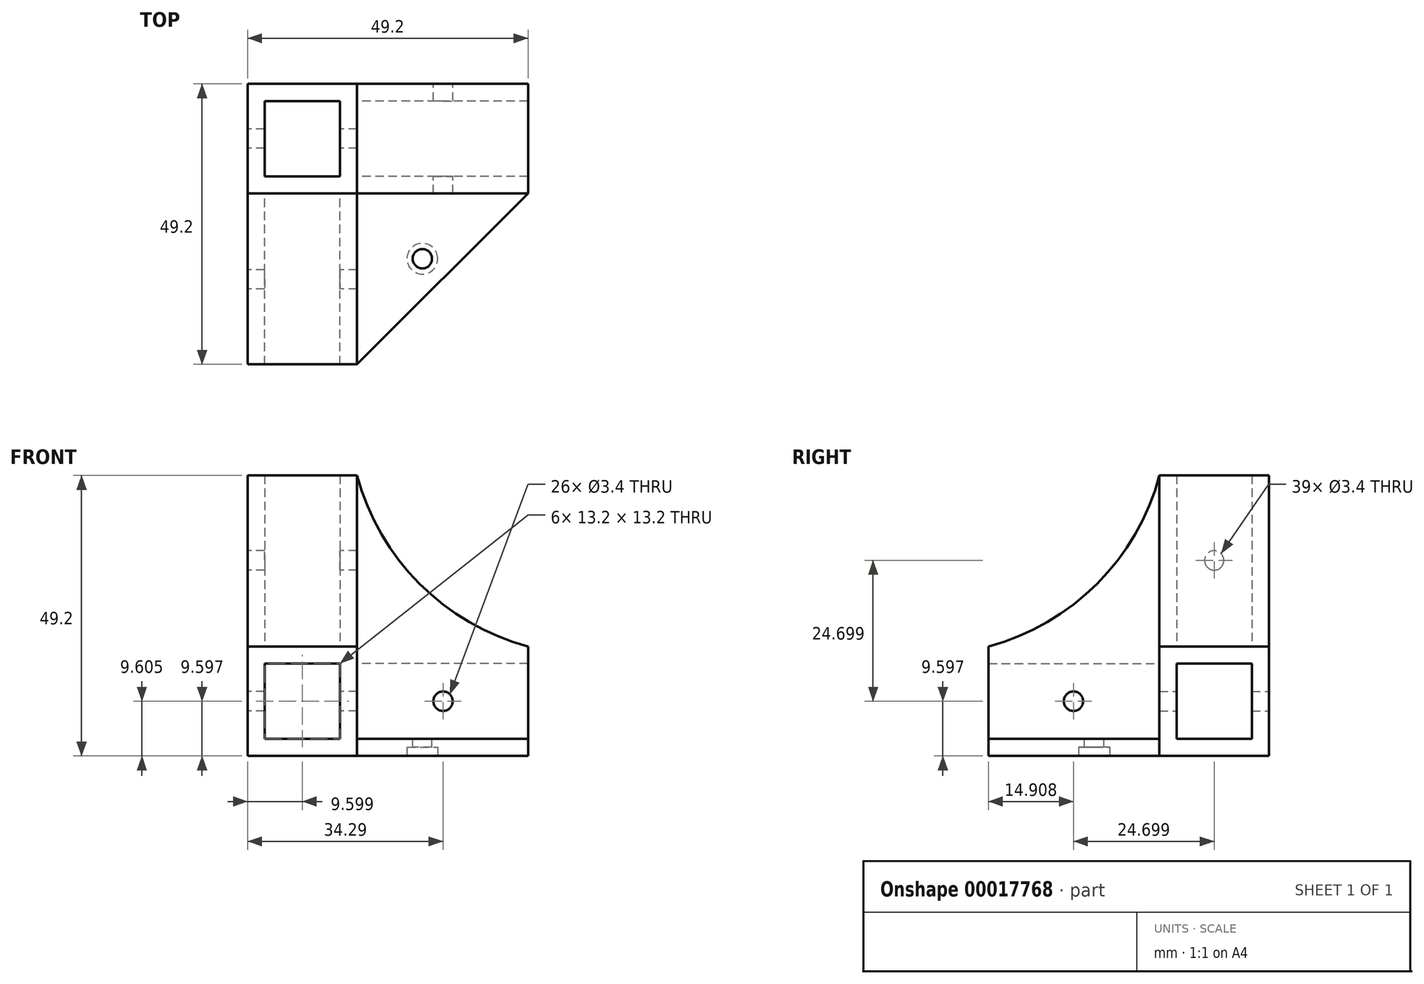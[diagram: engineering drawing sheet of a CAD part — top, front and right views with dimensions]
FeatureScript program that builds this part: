
annotation { "Feature Type Name" : "Feature", "Feature Type Description" : "" }
export const myFeature = defineFeature(function(context is Context, id is Id, definition is map)
    precondition{}
    {
        {
            var Q0;
            Q0=qCreatedBy(makeId("Front.planeOp"),FACE);
            var sketch = newSketch(context, id + "F0", { "sketchPlane" : qUnion([Q0])});
            skLineSegment(sketch, "E0.bottom", {"start": v(-58, 0.4) * mm, "end": v(-44.8, 0.4) * mm});
            skLineSegment(sketch, "E0.top", {"start": v(-58, -12.8) * mm, "end": v(-44.8, -12.8) * mm});
            skLineSegment(sketch, "E0.left", {"start": v(-58, 0.4) * mm, "end": v(-58, -12.8) * mm});
            skLineSegment(sketch, "E0.right", {"start": v(-44.8, 0.4) * mm, "end": v(-44.8, -12.8) * mm});
            skLineSegment(sketch, "E1.0", {"start": v(-61, 3.4) * mm, "end": v(-41.8, 3.4) * mm});
            skLineSegment(sketch, "E1.1", {"start": v(-61, 3.4) * mm, "end": v(-61, -15.8) * mm});
            skLineSegment(sketch, "E1.2", {"start": v(-61, -15.8) * mm, "end": v(-41.8, -15.8) * mm});
            skLineSegment(sketch, "E1.3", {"start": v(-41.8, 3.4) * mm, "end": v(-41.8, -15.8) * mm});
            skSolve(sketch);
        }
        {
            var Q0;
            Q0=makeQuery(id+"F0.imprint","IMPRINT",FACE,{"disambiguationData":[TD([[makeQuery(id+"F0.imprint","IMPRINT",EDGE,{"derivedFrom":sQuery(id+"F0.wireOp",EDGE,"E0.bottom")}),1.0]])]});
            extrude(context, id + "F1", {"entities" : qUnion([Q0]), "depth" : 30 * mm});
        }
        {
            var Q0;
            Q0=makeQuery(id+"F1.opExtrude","SWEPT_FACE",FACE,{"disambiguationData":[OSD([sQuery(id+"F0.wireOp",EDGE,"E1.1")])]});
            var sketch = newSketch(context, id + "F2", { "sketchPlane" : qUnion([Q0])});
            skCircle(sketch, "E2", {"center": v(15.1, -6.2) * mm, "radius": 1.7 * mm});
            skSolve(sketch);
        }
        {
            var Q0;
            Q0=makeQuery(id+"F2.imprint","IMPRINT",FACE,{"disambiguationData":[TD([[makeQuery(id+"F2.imprint","IMPRINT",EDGE,{"derivedFrom":sQuery(id+"F2.wireOp",EDGE,"E2")}),1.0]])]});
            extrude(context, id + "F3", {"entities" : qUnion([Q0]), "operationType" : NewBodyOperationType.REMOVE, "oppositeDirection" : true, "depth" : 25 * mm});
        }
        {
            var Q0;
            Q0=makeQuery(id+"F1.opExtrude","SWEPT_BODY",BODY,{"disambiguationData":[OSD([sQuery(id+"F0.wireOp",EDGE,"E0.bottom"),sQuery(id+"F0.wireOp",EDGE,"E0.top"),sQuery(id+"F0.wireOp",EDGE,"E0.left"),sQuery(id+"F0.wireOp",EDGE,"E0.right"),sQuery(id+"F0.wireOp",EDGE,"E1.0"),sQuery(id+"F0.wireOp",EDGE,"E1.1"),sQuery(id+"F0.wireOp",EDGE,"E1.2"),sQuery(id+"F0.wireOp",EDGE,"E1.3")])]});
            var Q1;
            Q1=makeQuery(id+"F1.opExtrude","CAP_EDGE",EDGE,{"disambiguationData":[OSD([sQuery(id+"F0.wireOp",EDGE,"E1.3")])],"isStart":true});
            transform(context, id + "F4", {"entities" : qUnion([Q0]), "transformType" : TransformType.ROTATION, "transformAxis" : qUnion([Q1]), "angle" : 90 * degree, "oppositeDirection" : true, "makeCopy" : true});
        }
        {
            var Q0;
            Q0=makeQuery(id+"F1.opExtrude","SWEPT_BODY",BODY,{"disambiguationData":[OSD([sQuery(id+"F0.wireOp",EDGE,"E0.bottom"),sQuery(id+"F0.wireOp",EDGE,"E0.top"),sQuery(id+"F0.wireOp",EDGE,"E0.left"),sQuery(id+"F0.wireOp",EDGE,"E0.right"),sQuery(id+"F0.wireOp",EDGE,"E1.0"),sQuery(id+"F0.wireOp",EDGE,"E1.1"),sQuery(id+"F0.wireOp",EDGE,"E1.2"),sQuery(id+"F0.wireOp",EDGE,"E1.3")])]});
            var Q1;
            Q1=makeQuery(id+"F1.opExtrude","CAP_EDGE",EDGE,{"disambiguationData":[OSD([sQuery(id+"F0.wireOp",EDGE,"E1.0")])],"isStart":true});
            transform(context, id + "F5", {"entities" : qUnion([Q0]), "transformType" : TransformType.ROTATION, "transformAxis" : qUnion([Q1]), "angle" : 90 * degree, "oppositeDirection" : true, "makeCopy" : true});
        }
        {
            var Q0;
            Q0=makeQuery(id+"F4.opPattern","COPY",BODY,{"derivedFrom":makeQuery(id+"F1.opExtrude","SWEPT_BODY",BODY,{"disambiguationData":[OSD([sQuery(id+"F0.wireOp",EDGE,"E0.bottom"),sQuery(id+"F0.wireOp",EDGE,"E0.top"),sQuery(id+"F0.wireOp",EDGE,"E0.left"),sQuery(id+"F0.wireOp",EDGE,"E0.right"),sQuery(id+"F0.wireOp",EDGE,"E1.0"),sQuery(id+"F0.wireOp",EDGE,"E1.1"),sQuery(id+"F0.wireOp",EDGE,"E1.2"),sQuery(id+"F0.wireOp",EDGE,"E1.3")])]}),"instanceName":"1"});
            var Q1;
            Q1=makeQuery(id+"F4.opPattern","COPY",FACE,{"derivedFrom":makeQuery(id+"F1.opExtrude","SWEPT_FACE",FACE,{"disambiguationData":[OSD([sQuery(id+"F0.wireOp",EDGE,"E1.3")])]}),"instanceName":"1"});
            mirror(context, id + "F6", {"entities" : qUnion([Q0]), "mirrorPlane" : qUnion([Q1])});
        }
        {
            var Q0;
            Q0=makeQuery(id+"F4.opPattern","COPY",BODY,{"derivedFrom":makeQuery(id+"F1.opExtrude","SWEPT_BODY",BODY,{"disambiguationData":[OSD([sQuery(id+"F0.wireOp",EDGE,"E0.bottom"),sQuery(id+"F0.wireOp",EDGE,"E0.top"),sQuery(id+"F0.wireOp",EDGE,"E0.left"),sQuery(id+"F0.wireOp",EDGE,"E0.right"),sQuery(id+"F0.wireOp",EDGE,"E1.0"),sQuery(id+"F0.wireOp",EDGE,"E1.1"),sQuery(id+"F0.wireOp",EDGE,"E1.2"),sQuery(id+"F0.wireOp",EDGE,"E1.3")])]}),"instanceName":"1"});
            deleteBodies(context, id + "F7", {"entities" : qUnion([Q0])});
        }
        {
            var Q0;
            Q0=makeQuery(id+"F5.opPattern","COPY",BODY,{"derivedFrom":makeQuery(id+"F1.opExtrude","SWEPT_BODY",BODY,{"disambiguationData":[OSD([sQuery(id+"F0.wireOp",EDGE,"E0.bottom"),sQuery(id+"F0.wireOp",EDGE,"E0.top"),sQuery(id+"F0.wireOp",EDGE,"E0.left"),sQuery(id+"F0.wireOp",EDGE,"E0.right"),sQuery(id+"F0.wireOp",EDGE,"E1.0"),sQuery(id+"F0.wireOp",EDGE,"E1.1"),sQuery(id+"F0.wireOp",EDGE,"E1.2"),sQuery(id+"F0.wireOp",EDGE,"E1.3")])]}),"instanceName":"1"});
            var Q1;
            Q1=qCreatedBy(makeId("Front.planeOp"),FACE);
            mirror(context, id + "F8", {"entities" : qUnion([Q0]), "mirrorPlane" : qUnion([Q1])});
        }
        {
            var Q0;
            Q0=makeQuery(id+"F5.opPattern","COPY",BODY,{"derivedFrom":makeQuery(id+"F1.opExtrude","SWEPT_BODY",BODY,{"disambiguationData":[OSD([sQuery(id+"F0.wireOp",EDGE,"E0.bottom"),sQuery(id+"F0.wireOp",EDGE,"E0.top"),sQuery(id+"F0.wireOp",EDGE,"E0.left"),sQuery(id+"F0.wireOp",EDGE,"E0.right"),sQuery(id+"F0.wireOp",EDGE,"E1.0"),sQuery(id+"F0.wireOp",EDGE,"E1.1"),sQuery(id+"F0.wireOp",EDGE,"E1.2"),sQuery(id+"F0.wireOp",EDGE,"E1.3")])]}),"instanceName":"1"});
            deleteBodies(context, id + "F9", {"entities" : qUnion([Q0])});
        }
        {
            var Q0;
            Q0=makeQuery(id+"F0.imprint","IMPRINT",FACE,{"disambiguationData":[TD([[makeQuery(id+"F0.imprint","IMPRINT",EDGE,{"derivedFrom":sQuery(id+"F0.wireOp",EDGE,"E0.bottom")}),1.0]])]});
            var Q1;
            Q1=sQuery(id+"F0.wireOp",EDGE,"E1.1");
            var Q2;
            Q2=sQuery(id+"F0.wireOp",EDGE,"E1.0");
            var Q3;
            Q3=sQuery(id+"F0.wireOp",EDGE,"E1.3");
            var Q4;
            Q4=sQuery(id+"F0.wireOp",EDGE,"E1.2");
            var Q5;
            Q5=makeQuery(id+"F8.opPattern","COPY",FACE,{"derivedFrom":makeQuery(id+"F5.opPattern","COPY",FACE,{"derivedFrom":makeQuery(id+"F1.opExtrude","SWEPT_FACE",FACE,{"disambiguationData":[OSD([sQuery(id+"F0.wireOp",EDGE,"E1.2")])]}),"instanceName":"1"}),"instanceName":"1"});
            extrude(context, id + "F10", {"entities" : qUnion([Q0]), "surfaceEntities" : qUnion([Q1, Q2, Q3, Q4]), "endBound" : BoundingType.UP_TO_SURFACE, "oppositeDirection" : true, "endBoundEntityFace" : qUnion([Q5]), "depth" : 21.53 * mm});
        }
        {
            var Q0;
            Q0=makeQuery(id+"F0.imprint","IMPRINT",FACE,{"disambiguationData":[TD([[makeQuery(id+"F0.imprint","IMPRINT",EDGE,{"derivedFrom":sQuery(id+"F0.wireOp",EDGE,"E0.bottom")}),-1.0]])]});
            var Q1;
            Q1=makeQuery(id+"F10.opExtrude","CAP_FACE",FACE,{"disambiguationData":[OSD([sQuery(id+"F0.wireOp",EDGE,"E0.bottom"),sQuery(id+"F0.wireOp",EDGE,"E0.top"),sQuery(id+"F0.wireOp",EDGE,"E0.left"),sQuery(id+"F0.wireOp",EDGE,"E0.right"),sQuery(id+"F0.wireOp",EDGE,"E1.0"),sQuery(id+"F0.wireOp",EDGE,"E1.1"),sQuery(id+"F0.wireOp",EDGE,"E1.2"),sQuery(id+"F0.wireOp",EDGE,"E1.3")])],"isStart":false});
            extrude(context, id + "F11", {"entities" : qUnion([Q0]), "endBound" : BoundingType.UP_TO_SURFACE, "oppositeDirection" : true, "endBoundEntityFace" : qUnion([Q1]), "depth" : 25 * mm});
        }
        {
            var Q0;
            Q0=makeQuery(id+"F10.opExtrude","SWEPT_FACE",FACE,{"disambiguationData":[OSD([sQuery(id+"F0.wireOp",EDGE,"E1.1")])]});
            var sketch = newSketch(context, id + "F12", { "sketchPlane" : qUnion([Q0])});
            skArc(sketch, "E3", {"start": v(0, 33.4) * mm, "mid": v(10.97, 14.38) * mm, "end": v(30, 3.4) * mm});
            skLineSegment(sketch, "E4", {"start": v(0, 33.4) * mm, "end": v(0, 3.4) * mm});
            skLineSegment(sketch, "E5", {"start": v(0, 3.4) * mm, "end": v(30, 3.4) * mm});
            skSolve(sketch);
        }
        {
            var Q0;
            Q0=makeQuery(id+"F12.imprint","IMPRINT",FACE,{"disambiguationData":[TD([[makeQuery(id+"F12.imprint","IMPRINT",EDGE,{"derivedFrom":sQuery(id+"F12.wireOp",EDGE,"E3")}),-1.0]])]});
            var Q1;
            Q1=makeQuery(id+"F8.opPattern","COPY",FACE,{"derivedFrom":makeQuery(id+"F5.opPattern","COPY",FACE,{"derivedFrom":makeQuery(id+"F1.opExtrude","SWEPT_FACE",FACE,{"disambiguationData":[OSD([sQuery(id+"F0.wireOp",EDGE,"E1.3")])]}),"instanceName":"1"}),"instanceName":"1"});
            extrude(context, id + "F13", {"entities" : qUnion([Q0]), "endBound" : BoundingType.UP_TO_SURFACE, "oppositeDirection" : true, "endBoundEntityFace" : qUnion([Q1]), "depth" : 25 * mm});
        }
        {
            var Q0;
            Q0=makeQuery(id+"F13.opExtrude","SWEPT_BODY",BODY,{"disambiguationData":[OSD([sQuery(id+"F12.wireOp",EDGE,"E3"),sQuery(id+"F12.wireOp",EDGE,"E4"),sQuery(id+"F12.wireOp",EDGE,"E5")])]});
            var Q1;
            Q1=makeQuery(id+"F8.opPattern","COPY",EDGE,{"derivedFrom":makeQuery(id+"F5.opPattern","COPY",EDGE,{"derivedFrom":makeQuery(id+"F1.opExtrude","SWEPT_EDGE",EDGE,{"disambiguationData":[OSD([sQuery(id+"F0.wireOp",EDGE,"E1.0"),sQuery(id+"F0.wireOp",EDGE,"E1.3")])]}),"instanceName":"1"}),"instanceName":"1"});
            transform(context, id + "F14", {"entities" : qUnion([Q0]), "transformType" : TransformType.ROTATION, "transformAxis" : qUnion([Q1]), "angle" : 90 * degree, "oppositeDirection" : true, "makeCopy" : true});
        }
        {
            var Q0;
            Q0=makeQuery(id+"F14.opPattern","COPY",FACE,{"derivedFrom":makeQuery(id+"F13.opExtrude","CAP_FACE",FACE,{"disambiguationData":[OSD([sQuery(id+"F12.wireOp",EDGE,"E3"),sQuery(id+"F12.wireOp",EDGE,"E4"),sQuery(id+"F12.wireOp",EDGE,"E5")])],"isStart":false}),"instanceName":"1"});
            var Q1;
            Q1=makeQuery(id+"F8.opPattern","COPY",FACE,{"derivedFrom":makeQuery(id+"F5.opPattern","COPY",FACE,{"derivedFrom":makeQuery(id+"F1.opExtrude","SWEPT_FACE",FACE,{"disambiguationData":[OSD([sQuery(id+"F0.wireOp",EDGE,"E1.2")])]}),"instanceName":"1"}),"instanceName":"1"});
            var Q2;
            Q2=makeQuery(id+"F6.opPattern","COPY",BODY,{"derivedFrom":makeQuery(id+"F4.opPattern","COPY",BODY,{"derivedFrom":makeQuery(id+"F1.opExtrude","SWEPT_BODY",BODY,{"disambiguationData":[OSD([sQuery(id+"F0.wireOp",EDGE,"E0.bottom"),sQuery(id+"F0.wireOp",EDGE,"E0.top"),sQuery(id+"F0.wireOp",EDGE,"E0.left"),sQuery(id+"F0.wireOp",EDGE,"E0.right"),sQuery(id+"F0.wireOp",EDGE,"E1.0"),sQuery(id+"F0.wireOp",EDGE,"E1.1"),sQuery(id+"F0.wireOp",EDGE,"E1.2"),sQuery(id+"F0.wireOp",EDGE,"E1.3")])]}),"instanceName":"1"}),"instanceName":"1"});
            extrude(context, id + "F15", {"entities" : qUnion([Q0]), "endBound" : BoundingType.UP_TO_SURFACE, "endBoundEntityFace" : qUnion([Q1]), "endBoundEntityBody" : qUnion([Q2]), "depth" : 30 * mm});
        }
        {
            var Q0;
            Q0=makeQuery(id+"F14.opPattern","COPY",BODY,{"derivedFrom":makeQuery(id+"F13.opExtrude","SWEPT_BODY",BODY,{"disambiguationData":[OSD([sQuery(id+"F12.wireOp",EDGE,"E3"),sQuery(id+"F12.wireOp",EDGE,"E4"),sQuery(id+"F12.wireOp",EDGE,"E5")])]}),"instanceName":"1"});
            deleteBodies(context, id + "F16", {"entities" : qUnion([Q0])});
        }
        {
            var Q0;
            Q0=makeQuery(id+"F1.opExtrude","SWEPT_FACE",FACE,{"disambiguationData":[OSD([sQuery(id+"F0.wireOp",EDGE,"E1.2")])]});
            var sketch = newSketch(context, id + "F17", { "sketchPlane" : qUnion([Q0])});
            skLineSegment(sketch, "E6", {"start": v(-41.8, 30) * mm, "end": v(-11.8, 0) * mm});
            skLineSegment(sketch, "E7", {"start": v(-11.8, 0) * mm, "end": v(-41.8, 0) * mm});
            skLineSegment(sketch, "E8", {"start": v(-41.8, 0) * mm, "end": v(-41.8, 30) * mm});
            skSolve(sketch);
        }
        {
            var Q0;
            Q0=makeQuery(id+"F17.imprint","IMPRINT",FACE,{"disambiguationData":[TD([[makeQuery(id+"F17.imprint","IMPRINT",EDGE,{"derivedFrom":sQuery(id+"F17.wireOp",EDGE,"E6")}),-1.0]])]});
            extrude(context, id + "F18", {"entities" : qUnion([Q0]), "oppositeDirection" : true, "depth" : 3 * mm});
        }
        {
            var Q0;
            Q0=makeQuery(id+"F8.opPattern","COPY",BODY,{"derivedFrom":makeQuery(id+"F5.opPattern","COPY",BODY,{"derivedFrom":makeQuery(id+"F1.opExtrude","SWEPT_BODY",BODY,{"disambiguationData":[OSD([sQuery(id+"F0.wireOp",EDGE,"E0.bottom"),sQuery(id+"F0.wireOp",EDGE,"E0.top"),sQuery(id+"F0.wireOp",EDGE,"E0.left"),sQuery(id+"F0.wireOp",EDGE,"E0.right"),sQuery(id+"F0.wireOp",EDGE,"E1.0"),sQuery(id+"F0.wireOp",EDGE,"E1.1"),sQuery(id+"F0.wireOp",EDGE,"E1.2"),sQuery(id+"F0.wireOp",EDGE,"E1.3")])]}),"instanceName":"1"}),"instanceName":"1"});
            var Q1;
            Q1=makeQuery(id+"F13.opExtrude","SWEPT_BODY",BODY,{"disambiguationData":[OSD([sQuery(id+"F12.wireOp",EDGE,"E3"),sQuery(id+"F12.wireOp",EDGE,"E4"),sQuery(id+"F12.wireOp",EDGE,"E5")])]});
            var Q2;
            Q2=makeQuery(id+"F15.opExtrude","SWEPT_BODY",BODY,{"disambiguationData":[OSD([sQuery(id+"F12.wireOp",EDGE,"E3"),sQuery(id+"F12.wireOp",EDGE,"E4"),sQuery(id+"F12.wireOp",EDGE,"E5")])]});
            var Q3;
            Q3=makeQuery(id+"F6.opPattern","COPY",BODY,{"derivedFrom":makeQuery(id+"F4.opPattern","COPY",BODY,{"derivedFrom":makeQuery(id+"F1.opExtrude","SWEPT_BODY",BODY,{"disambiguationData":[OSD([sQuery(id+"F0.wireOp",EDGE,"E0.bottom"),sQuery(id+"F0.wireOp",EDGE,"E0.top"),sQuery(id+"F0.wireOp",EDGE,"E0.left"),sQuery(id+"F0.wireOp",EDGE,"E0.right"),sQuery(id+"F0.wireOp",EDGE,"E1.0"),sQuery(id+"F0.wireOp",EDGE,"E1.1"),sQuery(id+"F0.wireOp",EDGE,"E1.2"),sQuery(id+"F0.wireOp",EDGE,"E1.3")])]}),"instanceName":"1"}),"instanceName":"1"});
            var Q4;
            Q4=makeQuery(id+"F1.opExtrude","SWEPT_BODY",BODY,{"disambiguationData":[OSD([sQuery(id+"F0.wireOp",EDGE,"E0.bottom"),sQuery(id+"F0.wireOp",EDGE,"E0.top"),sQuery(id+"F0.wireOp",EDGE,"E0.left"),sQuery(id+"F0.wireOp",EDGE,"E0.right"),sQuery(id+"F0.wireOp",EDGE,"E1.0"),sQuery(id+"F0.wireOp",EDGE,"E1.1"),sQuery(id+"F0.wireOp",EDGE,"E1.2"),sQuery(id+"F0.wireOp",EDGE,"E1.3")])]});
            var Q5;
            Q5=makeQuery(id+"F18.opExtrude","SWEPT_BODY",BODY,{"disambiguationData":[OSD([sQuery(id+"F17.wireOp",EDGE,"E6"),sQuery(id+"F17.wireOp",EDGE,"E7"),sQuery(id+"F17.wireOp",EDGE,"E8")])]});
            var Q6;
            Q6=makeQuery(id+"F10.opExtrude","SWEPT_BODY",BODY,{"disambiguationData":[OSD([sQuery(id+"F0.wireOp",EDGE,"E0.bottom"),sQuery(id+"F0.wireOp",EDGE,"E0.top"),sQuery(id+"F0.wireOp",EDGE,"E0.left"),sQuery(id+"F0.wireOp",EDGE,"E0.right"),sQuery(id+"F0.wireOp",EDGE,"E1.0"),sQuery(id+"F0.wireOp",EDGE,"E1.1"),sQuery(id+"F0.wireOp",EDGE,"E1.2"),sQuery(id+"F0.wireOp",EDGE,"E1.3")])]});
            var Q7;
            Q7=makeQuery(id+"F11.opExtrude","SWEPT_BODY",BODY,{"disambiguationData":[OSD([sQuery(id+"F0.wireOp",EDGE,"E0.bottom"),sQuery(id+"F0.wireOp",EDGE,"E0.top"),sQuery(id+"F0.wireOp",EDGE,"E0.left"),sQuery(id+"F0.wireOp",EDGE,"E0.right")])]});
            booleanBodies(context, id + "F19", {"operationType" : BooleanOperationType.UNION, "tools" : qUnion([Q0, Q1, Q2, Q3, Q4, Q5, Q6, Q7])});
        }
        {
            var Q0;
            Q0=makeQuery(id+"F18.opExtrude","CAP_FACE",FACE,{"disambiguationData":[OSD([sQuery(id+"F17.wireOp",EDGE,"E6"),sQuery(id+"F17.wireOp",EDGE,"E7"),sQuery(id+"F17.wireOp",EDGE,"E8")])],"isStart":false});
            var sketch = newSketch(context, id + "F20", { "sketchPlane" : qUnion([Q0])});
            skCircle(sketch, "E9", {"center": v(-30.34, -11.46) * mm, "radius": 1.7 * mm});
            skLineSegment(sketch, "E10", {"start": v(-41.8, 0) * mm, "end": v(-26.8, -15) * mm, "construction": true});
            skLineSegment(sketch, "E11", {"start": v(-26.8, -15) * mm, "end": v(-30.34, -11.46) * mm, "construction": true});
            skLineSegment(sketch, "E12.0", {"start": v(-16.8, 14.2) * mm, "end": v(-16.8, 2.07) * mm});
            skLineSegment(sketch, "E12.1", {"start": v(-56, 14.2) * mm, "end": v(-16.8, 14.2) * mm});
            skLineSegment(sketch, "E12.2", {"start": v(-56, -25) * mm, "end": v(-56, 14.2) * mm});
            skLineSegment(sketch, "E12.3", {"start": v(-43.87, -25) * mm, "end": v(-56, -25) * mm});
            skLineSegment(sketch, "E12.4", {"start": v(-16.8, 2.07) * mm, "end": v(-43.87, -25) * mm});
            skSolve(sketch);
        }
        {
            var Q0;
            Q0=makeQuery(id+"F20.imprint","IMPRINT",FACE,{"disambiguationData":[TD([[makeQuery(id+"F20.imprint","IMPRINT",EDGE,{"derivedFrom":sQuery(id+"F20.wireOp",EDGE,"E9")}),1.0]])]});
            extrude(context, id + "F21", {"entities" : qUnion([Q0]), "operationType" : NewBodyOperationType.REMOVE, "oppositeDirection" : true, "depth" : 25 * mm});
        }
        {
            var Q0;
            {var subQ0=sQuery(id+"F0.wireOp",EDGE,"E1.2");var subQ1=makeQuery(id+"F1.opExtrude","SWEPT_FACE",FACE,{"disambiguationData":[OSD([subQ0])]});Q0=makeQuery(id+"F19.opBoolean","MERGE",FACE,{"derivedFrom":[subQ1,makeQuery(id+"F6.opPattern","COPY",FACE,{"derivedFrom":makeQuery(id+"F4.opPattern","COPY",FACE,{"derivedFrom":subQ1,"instanceName":"1"}),"instanceName":"1"}),makeQuery(id+"F10.opExtrude","SWEPT_FACE",FACE,{"disambiguationData":[OSD([subQ0])]}),makeQuery(id+"F18.opExtrude","CAP_FACE",FACE,{"disambiguationData":[OSD([sQuery(id+"F17.wireOp",EDGE,"E6"),sQuery(id+"F17.wireOp",EDGE,"E7"),sQuery(id+"F17.wireOp",EDGE,"E8")])],"isStart":true})]});}
            var sketch = newSketch(context, id + "F22", { "sketchPlane" : qUnion([Q0])});
            skCircle(sketch, "E13.0", {"center": v(-30.34, 11.46) * mm, "radius": 1.7 * mm});
            skCircle(sketch, "E14.0", {"center": v(-30.34, 11.46) * mm, "radius": 2.7 * mm});
            skSolve(sketch);
        }
        {
            var Q0;
            Q0=makeQuery(id+"F22.imprint","IMPRINT",FACE,{"disambiguationData":[TD([[makeQuery(id+"F22.imprint","IMPRINT",EDGE,{"derivedFrom":sQuery(id+"F22.wireOp",EDGE,"E13.0")}),1.0]])]});
            extrude(context, id + "F23", {"entities" : qUnion([Q0]), "operationType" : NewBodyOperationType.REMOVE, "oppositeDirection" : true, "depth" : 1.5 * mm});
        }
    });
